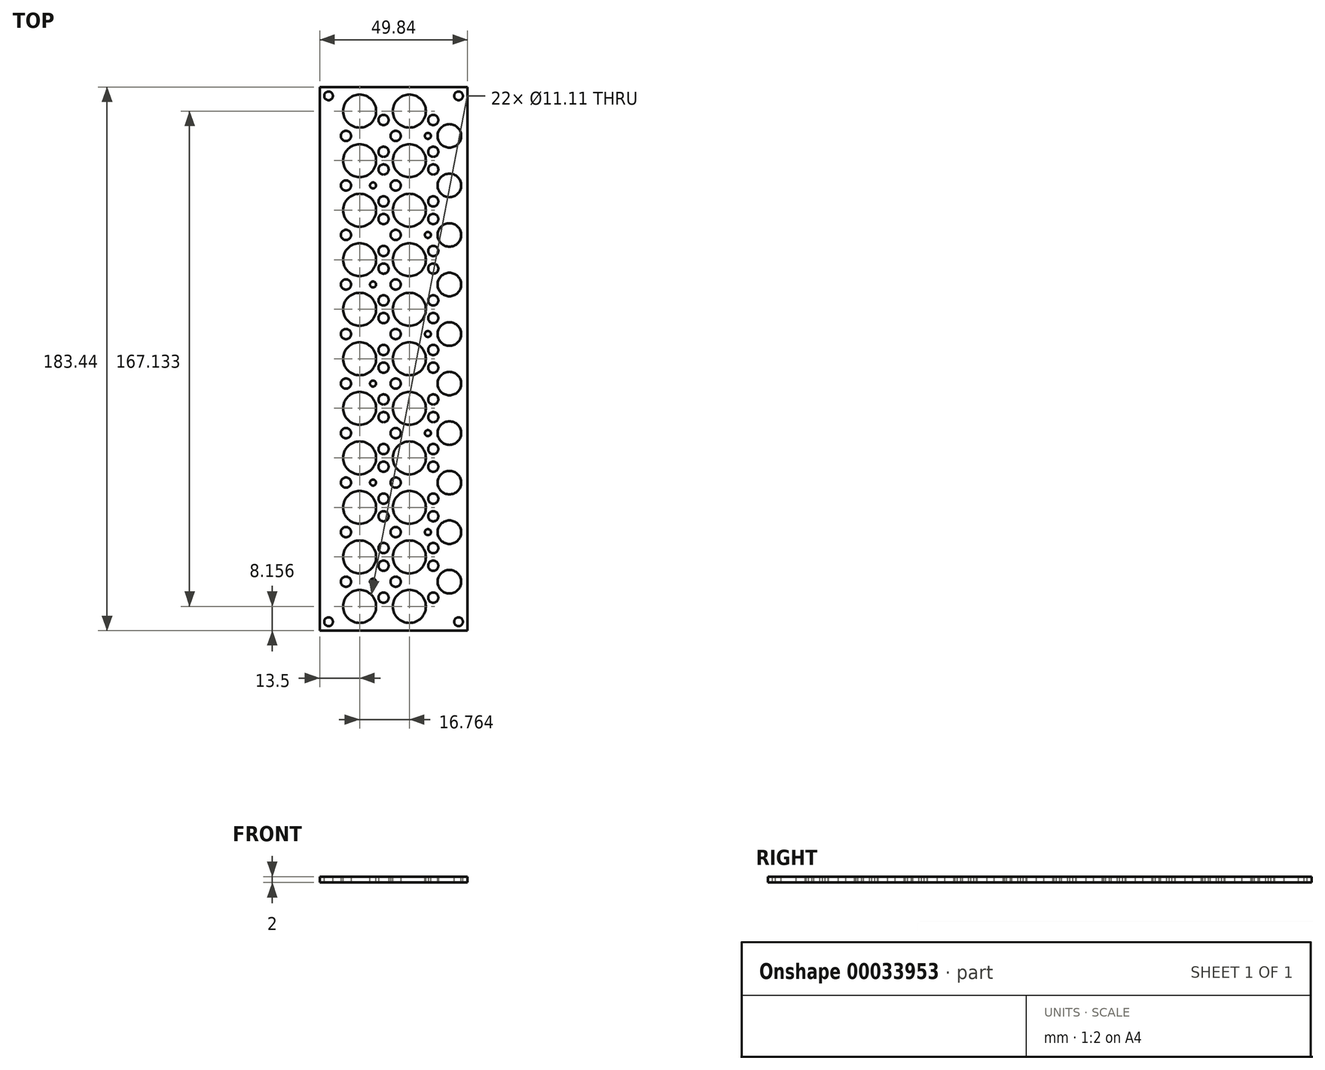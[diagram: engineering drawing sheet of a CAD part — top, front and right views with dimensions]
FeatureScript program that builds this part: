
annotation { "Feature Type Name" : "Feature", "Feature Type Description" : "" }
export const myFeature = defineFeature(function(context is Context, id is Id, definition is map)
    precondition{}
    {
        {
            var Q0;
            Q0=qCreatedBy(makeId("Top.planeOp"),FACE);
            var sketch = newSketch(context, id + "F0", { "sketchPlane" : qUnion([Q0])});
            skLineSegment(sketch, "E0.right", {"start": v(46.84, -3) * mm, "end": v(46.84, 180.44) * mm});
            skLineSegment(sketch, "E0.left", {"start": v(-3, -3) * mm, "end": v(-3, 180.44) * mm});
            skLineSegment(sketch, "E0.top", {"start": v(-3, 180.44) * mm, "end": v(46.84, 180.44) * mm});
            skLineSegment(sketch, "E0.bottom", {"start": v(-3, -3) * mm, "end": v(46.84, -3) * mm});
            skPoint(sketch, "E1.rect.middle", {"position": v(5.88, 30.23) * mm});
            skPoint(sketch, "E2.rect.middle", {"position": v(35.3, 8.14) * mm});
            skPoint(sketch, "E3.rect.middle", {"position": v(35.3, 24.85) * mm});
            skPoint(sketch, "E4.rect.middle", {"position": v(18.54, 24.85) * mm});
            skPoint(sketch, "E5.rect.middle", {"position": v(35.3, 18.89) * mm});
            skPoint(sketch, "E6.rect.middle", {"position": v(22.64, 13.51) * mm});
            skPoint(sketch, "E7.rect.middle", {"position": v(35.3, 35.6) * mm});
            skPoint(sketch, "E8.rect.middle", {"position": v(18.54, 8.14) * mm});
            skPoint(sketch, "E9.rect.middle", {"position": v(18.54, 35.6) * mm});
            skPoint(sketch, "E10.rect.middle", {"position": v(5.88, 13.51) * mm});
            skPoint(sketch, "E11.rect.middle", {"position": v(22.64, 30.23) * mm});
            skPoint(sketch, "E12.rect.middle", {"position": v(18.54, 18.89) * mm});
            skCircle(sketch, "E13", {"center": v(5.88, 13.51) * mm, "radius": 1.73 * mm});
            skCircle(sketch, "E14", {"center": v(18.54, 8.14) * mm, "radius": 1.73 * mm});
            skCircle(sketch, "E15", {"center": v(18.54, 18.89) * mm, "radius": 1.73 * mm});
            skCircle(sketch, "E16", {"center": v(22.64, 13.51) * mm, "radius": 1.73 * mm});
            skCircle(sketch, "E17", {"center": v(35.3, 8.14) * mm, "radius": 1.73 * mm});
            skCircle(sketch, "E18", {"center": v(35.3, 18.89) * mm, "radius": 1.73 * mm});
            skCircle(sketch, "E19", {"center": v(35.3, 24.85) * mm, "radius": 1.73 * mm});
            skCircle(sketch, "E20", {"center": v(35.3, 35.6) * mm, "radius": 1.73 * mm});
            skCircle(sketch, "E21", {"center": v(22.64, 30.23) * mm, "radius": 1.73 * mm});
            skCircle(sketch, "E22", {"center": v(18.54, 35.6) * mm, "radius": 1.73 * mm});
            skCircle(sketch, "E23", {"center": v(18.54, 24.85) * mm, "radius": 1.73 * mm});
            skCircle(sketch, "E24", {"center": v(5.88, 30.23) * mm, "radius": 1.73 * mm});
            skPoint(sketch, "E25.rect.middle", {"position": v(18.54, 69.03) * mm});
            skPoint(sketch, "E26.rect.middle", {"position": v(35.3, 41.56) * mm});
            skPoint(sketch, "E27.rect.middle", {"position": v(35.3, 52.32) * mm});
            skPoint(sketch, "E28.rect.middle", {"position": v(5.88, 46.94) * mm});
            skPoint(sketch, "E29.rect.middle", {"position": v(18.54, 52.32) * mm});
            skPoint(sketch, "E30.rect.middle", {"position": v(35.3, 69.03) * mm});
            skPoint(sketch, "E31.rect.middle", {"position": v(18.54, 41.56) * mm});
            skPoint(sketch, "E32.rect.middle", {"position": v(5.88, 63.65) * mm});
            skPoint(sketch, "E33.rect.middle", {"position": v(35.3, 58.28) * mm});
            skPoint(sketch, "E34.rect.middle", {"position": v(18.54, 58.28) * mm});
            skCircle(sketch, "E35", {"center": v(18.54, 41.56) * mm, "radius": 1.73 * mm});
            skCircle(sketch, "E36", {"center": v(35.3, 41.56) * mm, "radius": 1.73 * mm});
            skCircle(sketch, "E37", {"center": v(35.3, 52.32) * mm, "radius": 1.73 * mm});
            skCircle(sketch, "E38", {"center": v(35.3, 69.03) * mm, "radius": 1.73 * mm});
            skPoint(sketch, "E39.rect.middle", {"position": v(22.64, 63.65) * mm});
            skCircle(sketch, "E40", {"center": v(18.54, 69.03) * mm, "radius": 1.73 * mm});
            skPoint(sketch, "E41.rect.middle", {"position": v(22.64, 46.94) * mm});
            skCircle(sketch, "E42", {"center": v(18.54, 58.28) * mm, "radius": 1.73 * mm});
            skCircle(sketch, "E43", {"center": v(5.88, 63.65) * mm, "radius": 1.73 * mm});
            skCircle(sketch, "E44", {"center": v(5.88, 46.94) * mm, "radius": 1.73 * mm});
            skCircle(sketch, "E45", {"center": v(18.54, 52.32) * mm, "radius": 1.73 * mm});
            skCircle(sketch, "E46", {"center": v(35.3, 58.28) * mm, "radius": 1.73 * mm});
            skCircle(sketch, "E47", {"center": v(22.64, 63.65) * mm, "radius": 1.73 * mm});
            skCircle(sketch, "E48", {"center": v(22.64, 46.94) * mm, "radius": 1.73 * mm});
            skCircle(sketch, "E49", {"center": v(18.54, 135.88) * mm, "radius": 1.73 * mm});
            skPoint(sketch, "E50.rect.middle", {"position": v(35.3, 74.99) * mm});
            skPoint(sketch, "E51.rect.middle", {"position": v(22.64, 130.5) * mm});
            skPoint(sketch, "E52.rect.middle", {"position": v(35.3, 135.88) * mm});
            skPoint(sketch, "E53.rect.middle", {"position": v(5.88, 80.37) * mm});
            skCircle(sketch, "E54", {"center": v(18.54, 125.13) * mm, "radius": 1.73 * mm});
            skCircle(sketch, "E55", {"center": v(18.54, 119.17) * mm, "radius": 1.73 * mm});
            skCircle(sketch, "E56", {"center": v(35.3, 108.42) * mm, "radius": 1.73 * mm});
            skPoint(sketch, "E57.rect.middle", {"position": v(35.3, 125.13) * mm});
            skCircle(sketch, "E58", {"center": v(35.3, 125.13) * mm, "radius": 1.73 * mm});
            skCircle(sketch, "E59", {"center": v(35.3, 119.17) * mm, "radius": 1.73 * mm});
            skCircle(sketch, "E60", {"center": v(35.3, 74.99) * mm, "radius": 1.73 * mm});
            skPoint(sketch, "E61.rect.middle", {"position": v(5.88, 97.08) * mm});
            skCircle(sketch, "E62", {"center": v(22.64, 80.37) * mm, "radius": 1.73 * mm});
            skCircle(sketch, "E63", {"center": v(18.54, 85.74) * mm, "radius": 1.73 * mm});
            skPoint(sketch, "E64.rect.middle", {"position": v(18.54, 102.46) * mm});
            skPoint(sketch, "E65.rect.middle", {"position": v(22.64, 113.8) * mm});
            skCircle(sketch, "E66", {"center": v(18.54, 74.99) * mm, "radius": 1.73 * mm});
            skCircle(sketch, "E67", {"center": v(18.54, 91.7) * mm, "radius": 1.73 * mm});
            skCircle(sketch, "E68", {"center": v(5.88, 80.37) * mm, "radius": 1.73 * mm});
            skCircle(sketch, "E69", {"center": v(5.88, 97.08) * mm, "radius": 1.73 * mm});
            skPoint(sketch, "E70.rect.middle", {"position": v(35.3, 102.46) * mm});
            skCircle(sketch, "E71", {"center": v(18.54, 102.46) * mm, "radius": 1.73 * mm});
            skCircle(sketch, "E72", {"center": v(35.3, 135.88) * mm, "radius": 1.73 * mm});
            skCircle(sketch, "E73", {"center": v(22.64, 130.5) * mm, "radius": 1.73 * mm});
            skPoint(sketch, "E74.rect.middle", {"position": v(5.88, 113.8) * mm});
            skCircle(sketch, "E75", {"center": v(35.3, 85.74) * mm, "radius": 1.73 * mm});
            skPoint(sketch, "E76.rect.middle", {"position": v(18.54, 108.42) * mm});
            skPoint(sketch, "E77.rect.middle", {"position": v(22.64, 97.08) * mm});
            skCircle(sketch, "E78", {"center": v(5.88, 130.5) * mm, "radius": 1.73 * mm});
            skPoint(sketch, "E79.rect.middle", {"position": v(35.3, 91.7) * mm});
            skCircle(sketch, "E80", {"center": v(35.3, 91.7) * mm, "radius": 1.73 * mm});
            skCircle(sketch, "E81", {"center": v(35.3, 102.46) * mm, "radius": 1.73 * mm});
            skCircle(sketch, "E82", {"center": v(22.64, 97.08) * mm, "radius": 1.73 * mm});
            skCircle(sketch, "E83", {"center": v(22.64, 113.8) * mm, "radius": 1.73 * mm});
            skCircle(sketch, "E84", {"center": v(5.88, 113.8) * mm, "radius": 1.73 * mm});
            skCircle(sketch, "E85", {"center": v(18.54, 108.42) * mm, "radius": 1.73 * mm});
            skPoint(sketch, "E86.rect.middle", {"position": v(5.88, 147.22) * mm});
            skPoint(sketch, "E87.rect.middle", {"position": v(18.54, 152.6) * mm});
            skPoint(sketch, "E88.rect.middle", {"position": v(35.3, 169.3) * mm});
            skPoint(sketch, "E89.rect.middle", {"position": v(35.3, 141.84) * mm});
            skPoint(sketch, "E90.rect.middle", {"position": v(18.54, 141.84) * mm});
            skPoint(sketch, "E91.rect.middle", {"position": v(18.54, 169.3) * mm});
            skPoint(sketch, "E92.rect.middle", {"position": v(35.3, 152.6) * mm});
            skPoint(sketch, "E93.rect.middle", {"position": v(18.54, 158.56) * mm});
            skPoint(sketch, "E94.rect.middle", {"position": v(35.3, 158.56) * mm});
            skPoint(sketch, "E95.rect.middle", {"position": v(5.88, 163.93) * mm});
            skCircle(sketch, "E96", {"center": v(35.3, 141.84) * mm, "radius": 1.73 * mm});
            skCircle(sketch, "E97", {"center": v(35.3, 169.3) * mm, "radius": 1.73 * mm});
            skCircle(sketch, "E98", {"center": v(5.88, 163.93) * mm, "radius": 1.73 * mm});
            skCircle(sketch, "E99", {"center": v(18.54, 158.56) * mm, "radius": 1.73 * mm});
            skCircle(sketch, "E100", {"center": v(35.3, 158.56) * mm, "radius": 1.73 * mm});
            skCircle(sketch, "E101", {"center": v(35.3, 152.6) * mm, "radius": 1.73 * mm});
            skCircle(sketch, "E102", {"center": v(18.54, 169.3) * mm, "radius": 1.73 * mm});
            skCircle(sketch, "E103", {"center": v(5.88, 147.22) * mm, "radius": 1.73 * mm});
            skPoint(sketch, "E104.rect.middle", {"position": v(22.64, 147.22) * mm});
            skCircle(sketch, "E105", {"center": v(18.54, 152.6) * mm, "radius": 1.73 * mm});
            skCircle(sketch, "E106", {"center": v(18.54, 141.84) * mm, "radius": 1.73 * mm});
            skPoint(sketch, "E107.rect.middle", {"position": v(22.64, 163.93) * mm});
            skCircle(sketch, "E108", {"center": v(22.64, 147.22) * mm, "radius": 1.73 * mm});
            skCircle(sketch, "E109", {"center": v(22.64, 163.93) * mm, "radius": 1.73 * mm});
            skSolve(sketch);
        }
        {
            var Q0;
            Q0 = qSketchRegion(id + "F0", true);
            extrude(context, id + "F1", {"entities" : qUnion([Q0]), "depth" : 2 * mm});
        }
        {
            var Q0;
            Q0=makeQuery(id+"F1.opExtrude","CAP_FACE",FACE,{"disambiguationData":[OSD([sQuery(id+"F0.wireOp",EDGE,"E0.right"),sQuery(id+"F0.wireOp",EDGE,"E0.left"),sQuery(id+"F0.wireOp",EDGE,"E0.top"),sQuery(id+"F0.wireOp",EDGE,"E0.bottom"),sQuery(id+"F0.wireOp",EDGE,"E13"),sQuery(id+"F0.wireOp",EDGE,"E14"),sQuery(id+"F0.wireOp",EDGE,"E15"),sQuery(id+"F0.wireOp",EDGE,"E16"),sQuery(id+"F0.wireOp",EDGE,"E17"),sQuery(id+"F0.wireOp",EDGE,"E18"),sQuery(id+"F0.wireOp",EDGE,"E19"),sQuery(id+"F0.wireOp",EDGE,"E20"),sQuery(id+"F0.wireOp",EDGE,"E21"),sQuery(id+"F0.wireOp",EDGE,"E22"),sQuery(id+"F0.wireOp",EDGE,"E23"),sQuery(id+"F0.wireOp",EDGE,"E24"),sQuery(id+"F0.wireOp",EDGE,"E35"),sQuery(id+"F0.wireOp",EDGE,"E36"),sQuery(id+"F0.wireOp",EDGE,"E37"),sQuery(id+"F0.wireOp",EDGE,"E38"),sQuery(id+"F0.wireOp",EDGE,"E40"),sQuery(id+"F0.wireOp",EDGE,"E42"),sQuery(id+"F0.wireOp",EDGE,"E43"),sQuery(id+"F0.wireOp",EDGE,"E44"),sQuery(id+"F0.wireOp",EDGE,"E45"),sQuery(id+"F0.wireOp",EDGE,"E46"),sQuery(id+"F0.wireOp",EDGE,"E47"),sQuery(id+"F0.wireOp",EDGE,"E48"),sQuery(id+"F0.wireOp",EDGE,"E49"),sQuery(id+"F0.wireOp",EDGE,"E54"),sQuery(id+"F0.wireOp",EDGE,"E55"),sQuery(id+"F0.wireOp",EDGE,"E56"),sQuery(id+"F0.wireOp",EDGE,"E58"),sQuery(id+"F0.wireOp",EDGE,"E59"),sQuery(id+"F0.wireOp",EDGE,"E60"),sQuery(id+"F0.wireOp",EDGE,"E62"),sQuery(id+"F0.wireOp",EDGE,"E63"),sQuery(id+"F0.wireOp",EDGE,"E66"),sQuery(id+"F0.wireOp",EDGE,"E67"),sQuery(id+"F0.wireOp",EDGE,"E68"),sQuery(id+"F0.wireOp",EDGE,"E69"),sQuery(id+"F0.wireOp",EDGE,"E71"),sQuery(id+"F0.wireOp",EDGE,"E72"),sQuery(id+"F0.wireOp",EDGE,"E73"),sQuery(id+"F0.wireOp",EDGE,"E75"),sQuery(id+"F0.wireOp",EDGE,"E78"),sQuery(id+"F0.wireOp",EDGE,"E80"),sQuery(id+"F0.wireOp",EDGE,"E81"),sQuery(id+"F0.wireOp",EDGE,"E82"),sQuery(id+"F0.wireOp",EDGE,"E83"),sQuery(id+"F0.wireOp",EDGE,"E84"),sQuery(id+"F0.wireOp",EDGE,"E85"),sQuery(id+"F0.wireOp",EDGE,"E96"),sQuery(id+"F0.wireOp",EDGE,"E97"),sQuery(id+"F0.wireOp",EDGE,"E98"),sQuery(id+"F0.wireOp",EDGE,"E99"),sQuery(id+"F0.wireOp",EDGE,"E100"),sQuery(id+"F0.wireOp",EDGE,"E101"),sQuery(id+"F0.wireOp",EDGE,"E102"),sQuery(id+"F0.wireOp",EDGE,"E103"),sQuery(id+"F0.wireOp",EDGE,"E105"),sQuery(id+"F0.wireOp",EDGE,"E106"),sQuery(id+"F0.wireOp",EDGE,"E108"),sQuery(id+"F0.wireOp",EDGE,"E109")])],"isStart":false});
            var sketch = newSketch(context, id + "F2", { "sketchPlane" : qUnion([Q0])});
            skCircle(sketch, "E110", {"center": v(10.5, 21.87) * mm, "radius": 5.56 * mm});
            skCircle(sketch, "E111", {"center": v(40.76, 113.8) * mm, "radius": 3.97 * mm});
            skCircle(sketch, "E112", {"center": v(10.5, 138.86) * mm, "radius": 5.56 * mm});
            skCircle(sketch, "E113", {"center": v(27.26, 155.58) * mm, "radius": 5.56 * mm});
            skCircle(sketch, "E114", {"center": v(40.76, 97.08) * mm, "radius": 3.97 * mm});
            skCircle(sketch, "E115", {"center": v(27.26, 122.15) * mm, "radius": 5.56 * mm});
            skCircle(sketch, "E116", {"center": v(27.26, 38.58) * mm, "radius": 5.56 * mm});
            skCircle(sketch, "E117", {"center": v(10.5, 155.58) * mm, "radius": 5.56 * mm});
            skCircle(sketch, "E118", {"center": v(40.76, 147.22) * mm, "radius": 3.97 * mm});
            skCircle(sketch, "E119", {"center": v(10.5, 105.44) * mm, "radius": 5.56 * mm});
            skCircle(sketch, "E120", {"center": v(27.26, 105.44) * mm, "radius": 5.56 * mm});
            skCircle(sketch, "E121", {"center": v(10.5, 88.72) * mm, "radius": 5.56 * mm});
            skCircle(sketch, "E122", {"center": v(27.26, 88.72) * mm, "radius": 5.56 * mm});
            skCircle(sketch, "E123", {"center": v(10.5, 122.15) * mm, "radius": 5.56 * mm});
            skCircle(sketch, "E124", {"center": v(40.76, 130.5) * mm, "radius": 3.97 * mm});
            skCircle(sketch, "E125", {"center": v(27.26, 172.29) * mm, "radius": 5.56 * mm});
            skCircle(sketch, "E126", {"center": v(10.5, 5.16) * mm, "radius": 5.56 * mm});
            skCircle(sketch, "E127", {"center": v(27.26, 5.16) * mm, "radius": 5.56 * mm});
            skCircle(sketch, "E128", {"center": v(27.26, 21.87) * mm, "radius": 5.56 * mm});
            skCircle(sketch, "E129", {"center": v(40.76, 13.51) * mm, "radius": 3.97 * mm});
            skCircle(sketch, "E130", {"center": v(27.26, 55.3) * mm, "radius": 5.56 * mm});
            skCircle(sketch, "E131", {"center": v(40.76, 46.94) * mm, "radius": 3.97 * mm});
            skCircle(sketch, "E132", {"center": v(10.5, 38.58) * mm, "radius": 5.56 * mm});
            skCircle(sketch, "E133", {"center": v(40.76, 30.23) * mm, "radius": 3.97 * mm});
            skCircle(sketch, "E134", {"center": v(40.76, 63.65) * mm, "radius": 3.97 * mm});
            skCircle(sketch, "E135", {"center": v(10.5, 172.29) * mm, "radius": 5.56 * mm});
            skCircle(sketch, "E136", {"center": v(27.26, 72) * mm, "radius": 5.56 * mm});
            skCircle(sketch, "E137", {"center": v(10.5, 55.3) * mm, "radius": 5.56 * mm});
            skCircle(sketch, "E138", {"center": v(40.76, 80.37) * mm, "radius": 3.97 * mm});
            skCircle(sketch, "E139", {"center": v(27.26, 138.86) * mm, "radius": 5.56 * mm});
            skCircle(sketch, "E140", {"center": v(10.5, 72) * mm, "radius": 5.56 * mm});
            skCircle(sketch, "E141", {"center": v(40.76, 163.93) * mm, "radius": 3.97 * mm});
            skCircle(sketch, "E142", {"center": v(43.84, 0) * mm, "radius": 1.47 * mm});
            skCircle(sketch, "E143", {"center": v(0, 177.44) * mm, "radius": 1.47 * mm});
            skCircle(sketch, "E144", {"center": v(15, 13.51) * mm, "radius": 1.02 * mm});
            skCircle(sketch, "E145", {"center": v(33.5, 30.23) * mm, "radius": 1.02 * mm});
            skCircle(sketch, "E146", {"center": v(15, 46.94) * mm, "radius": 1.02 * mm});
            skCircle(sketch, "E147", {"center": v(33.5, 63.65) * mm, "radius": 1.02 * mm});
            skCircle(sketch, "E148", {"center": v(15, 80.37) * mm, "radius": 1.02 * mm});
            skCircle(sketch, "E149", {"center": v(33.5, 97.08) * mm, "radius": 1.02 * mm});
            skCircle(sketch, "E150", {"center": v(15, 113.8) * mm, "radius": 1.02 * mm});
            skCircle(sketch, "E151", {"center": v(33.5, 130.5) * mm, "radius": 1.02 * mm});
            skCircle(sketch, "E152", {"center": v(33.5, 163.93) * mm, "radius": 1.02 * mm});
            skCircle(sketch, "E153", {"center": v(15, 147.22) * mm, "radius": 1.02 * mm});
            skCircle(sketch, "E154", {"center": v(0, 0) * mm, "radius": 1.47 * mm});
            skCircle(sketch, "E155", {"center": v(43.84, 177.44) * mm, "radius": 1.47 * mm});
            skSolve(sketch);
        }
        {
            var Q0;
            Q0 = qSketchRegion(id + "F2", true);
            extrude(context, id + "F3", {"entities" : qUnion([Q0]), "operationType" : NewBodyOperationType.REMOVE, "oppositeDirection" : true, "depth" : 25 * mm});
        }
    });
